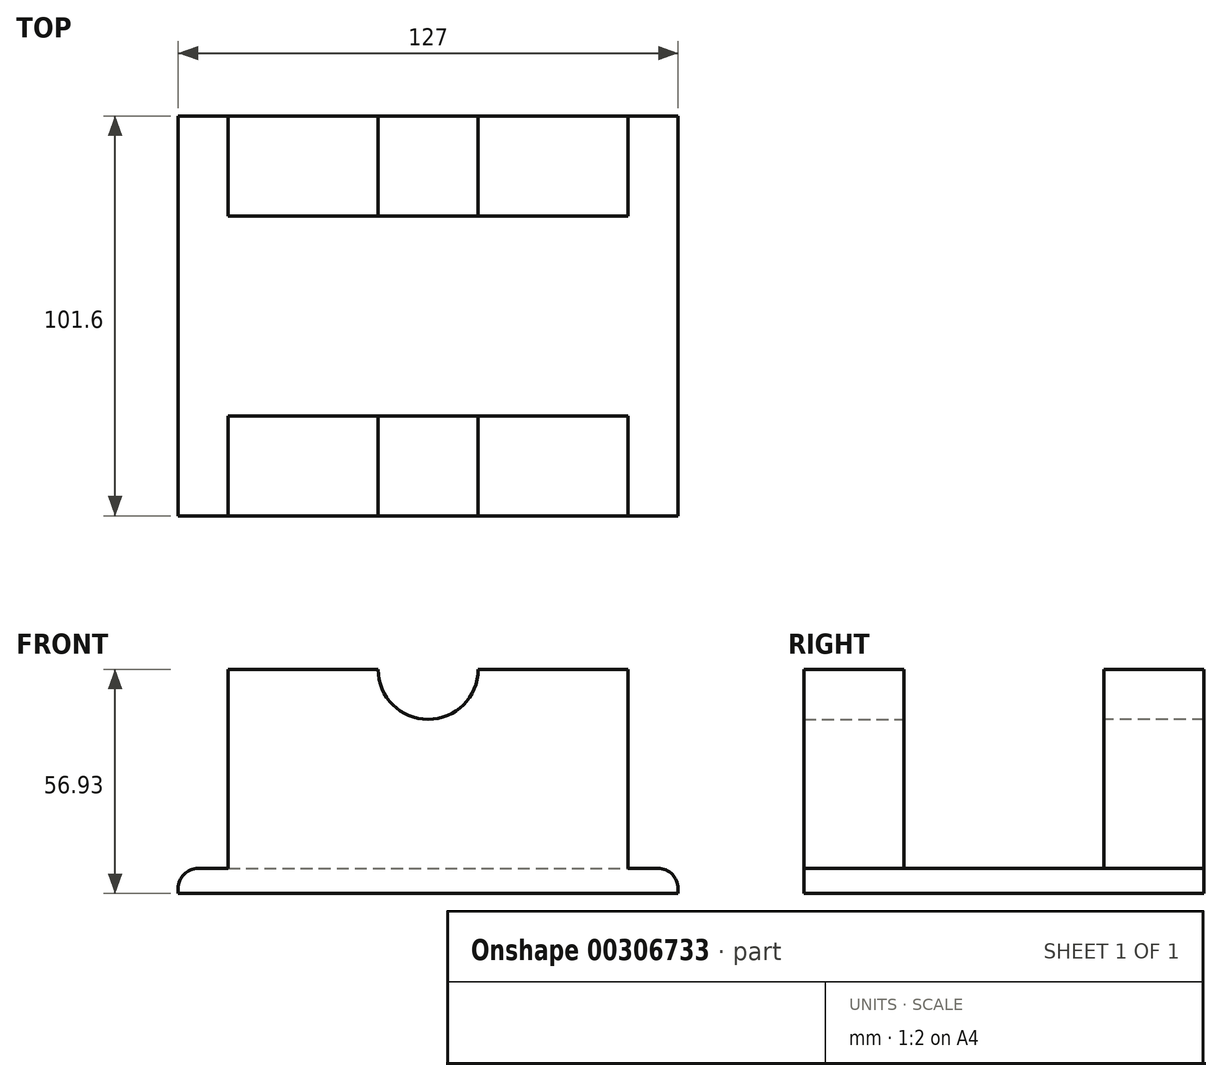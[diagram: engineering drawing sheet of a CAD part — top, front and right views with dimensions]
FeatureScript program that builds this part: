
annotation { "Feature Type Name" : "Feature", "Feature Type Description" : "" }
export const myFeature = defineFeature(function(context is Context, id is Id, definition is map)
    precondition{}
    {
        {
            var Q0;
            Q0=qCreatedBy(makeId("Top.planeOp"),FACE);
            var sketch = newSketch(context, id + "F0", { "sketchPlane" : qUnion([Q0])});
            skLineSegment(sketch, "E0.bottom", {"start": v(63.5, 50.8) * mm, "end": v(-63.5, 50.8) * mm});
            skLineSegment(sketch, "E0.top", {"start": v(63.5, -50.8) * mm, "end": v(-63.5, -50.8) * mm});
            skLineSegment(sketch, "E0.left", {"start": v(63.5, 50.8) * mm, "end": v(63.5, -50.8) * mm});
            skLineSegment(sketch, "E0.right", {"start": v(-63.5, 50.8) * mm, "end": v(-63.5, -50.8) * mm});
            skPoint(sketch, "E0.middle", {"position": v(0, 0) * mm});
            skSolve(sketch);
        }
        {
            var Q0;
            Q0=makeQuery(id+"F0.imprint","IMPRINT",FACE,{"disambiguationData":[TD([[makeQuery(id+"F0.imprint","IMPRINT",EDGE,{"derivedFrom":sQuery(id+"F0.wireOp",EDGE,"E0.bottom")}),1.0]])]});
            extrude(context, id + "F1", {"entities" : qUnion([Q0]), "depth" : 6.35 * mm});
        }
        {
            var Q0;
            Q0=qCreatedBy(makeId("Front.planeOp"),FACE);
            cPlane(context, id + "F2", {"entities" : qUnion([Q0]), "cplaneType" : CPlaneType.OFFSET, "offset" : 25.4 * mm, "width" : 152.4 * mm, "height" : 152.4 * mm});
        }
        {
            var Q0;
            Q0=qCreatedBy(id+"F2.planeOp",FACE);
            var sketch = newSketch(context, id + "F3", { "sketchPlane" : qUnion([Q0])});
            skLineSegment(sketch, "E1", {"start": v(50.8, 6.13) * mm, "end": v(-50.8, 6.13) * mm});
            skLineSegment(sketch, "E2", {"start": v(-50.8, 6.13) * mm, "end": v(-50.8, 56.93) * mm});
            skLineSegment(sketch, "E3", {"start": v(50.8, 6.13) * mm, "end": v(50.8, 56.93) * mm});
            skLineSegment(sketch, "E4", {"start": v(-50.8, 56.93) * mm, "end": v(-12.7, 56.93) * mm});
            skLineSegment(sketch, "E5", {"start": v(50.8, 56.93) * mm, "end": v(12.7, 56.93) * mm});
            skArc(sketch, "E6", {"start": v(-12.7, 56.93) * mm, "mid": v(0, 44.23) * mm, "end": v(12.7, 56.93) * mm});
            skSolve(sketch);
        }
        {
            var Q0;
            Q0=makeQuery(id+"F1.opExtrude","CAP_EDGE",EDGE,{"disambiguationData":[OSD([sQuery(id+"F0.wireOp",EDGE,"E0.left")])],"isStart":false});
            var Q1;
            Q1=makeQuery(id+"F1.opExtrude","CAP_EDGE",EDGE,{"disambiguationData":[OSD([sQuery(id+"F0.wireOp",EDGE,"E0.right")])],"isStart":false});
            fillet(context, id + "F4", {"entities" : qUnion([Q0, Q1]), "radius" : 5.08 * mm, "tangentPropagation" : true, "allowEdgeOverflow" : false});
        }
        {
            var Q0;
            Q0=makeQuery(id+"F3.imprint","IMPRINT",FACE,{"disambiguationData":[TD([[makeQuery(id+"F3.imprint","IMPRINT",EDGE,{"derivedFrom":sQuery(id+"F3.wireOp",EDGE,"E1")}),-1.0]])]});
            extrude(context, id + "F5", {"entities" : qUnion([Q0]), "operationType" : NewBodyOperationType.ADD, "depth" : 25.4 * mm});
        }
        {
            var Q0;
            Q0=makeQuery(id+"F1.opExtrude","SWEPT_BODY",BODY,{"disambiguationData":[OSD([sQuery(id+"F0.wireOp",EDGE,"E0.bottom"),sQuery(id+"F0.wireOp",EDGE,"E0.top"),sQuery(id+"F0.wireOp",EDGE,"E0.left"),sQuery(id+"F0.wireOp",EDGE,"E0.right")])]});
            var Q1;
            Q1=qCreatedBy(makeId("Front.planeOp"),FACE);
            mirror(context, id + "F6", {"operationType" : NewBodyOperationType.ADD, "entities" : qUnion([Q0]), "mirrorPlane" : qUnion([Q1])});
        }
    });
